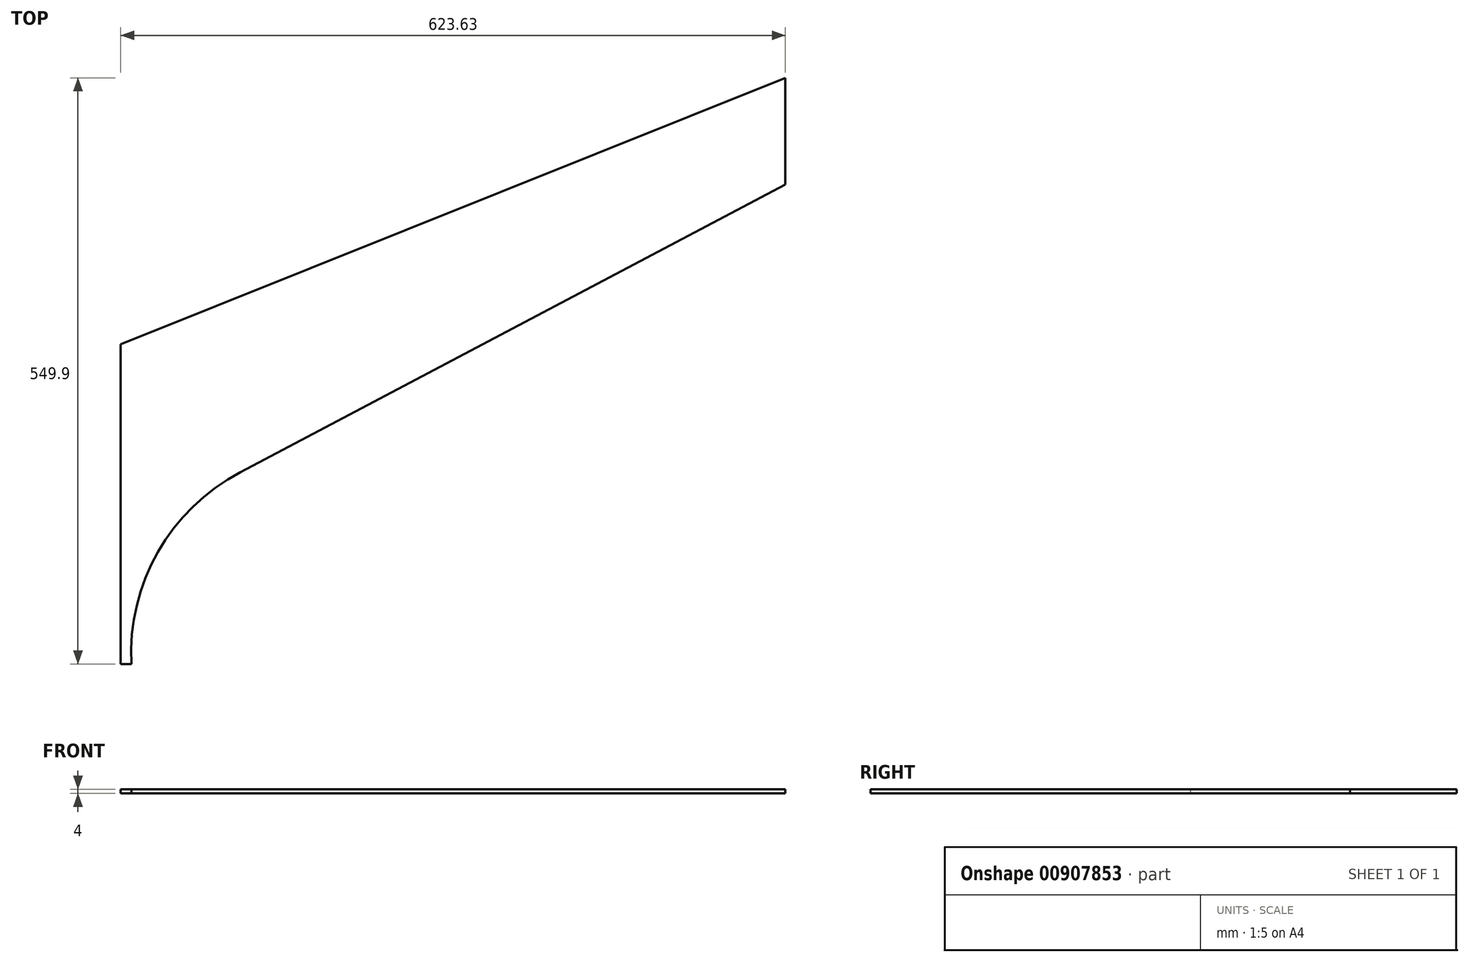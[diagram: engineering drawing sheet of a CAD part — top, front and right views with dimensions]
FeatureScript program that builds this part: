
annotation { "Feature Type Name" : "Feature", "Feature Type Description" : "" }
export const myFeature = defineFeature(function(context is Context, id is Id, definition is map)
    precondition{}
    {
        {
            var Q0;
            Q0=qCreatedBy(makeId("Top.planeOp"),FACE);
            var sketch = newSketch(context, id + "F0", { "sketchPlane" : qUnion([Q0])});
            skLineSegment(sketch, "E0", {"start": v(-66.34, -57.39) * mm, "end": v(445.02, 212.5) * mm});
            skLineSegment(sketch, "E1", {"start": v(445.02, 212.5) * mm, "end": v(445.02, 312.5) * mm});
            skArc(sketch, "E2", {"start": v(-66.34, -57.39) * mm, "mid": v(-143.76, -132.45) * mm, "end": v(-168.6, -237.39) * mm});
            skLineSegment(sketch, "E3", {"start": v(-168.6, -237.39) * mm, "end": v(-178.6, -237.39) * mm});
            skLineSegment(sketch, "E4", {"start": v(-178.6, -237.39) * mm, "end": v(-178.6, 62.61) * mm});
            skLineSegment(sketch, "E5", {"start": v(-178.6, 62.61) * mm, "end": v(445.02, 312.5) * mm});
            skSolve(sketch);
        }
        {
            var Q0;
            Q0=makeQuery(id+"F0.imprint","IMPRINT",FACE,{"disambiguationData":[TD([[makeQuery(id+"F0.imprint","IMPRINT",EDGE,{"derivedFrom":sQuery(id+"F0.wireOp",EDGE,"E0")}),1.0]])]});
            extrude(context, id + "F1", {"entities" : qUnion([Q0]), "depth" : 4 * mm, "offsetDistance" : 25 * mm});
        }
    });
